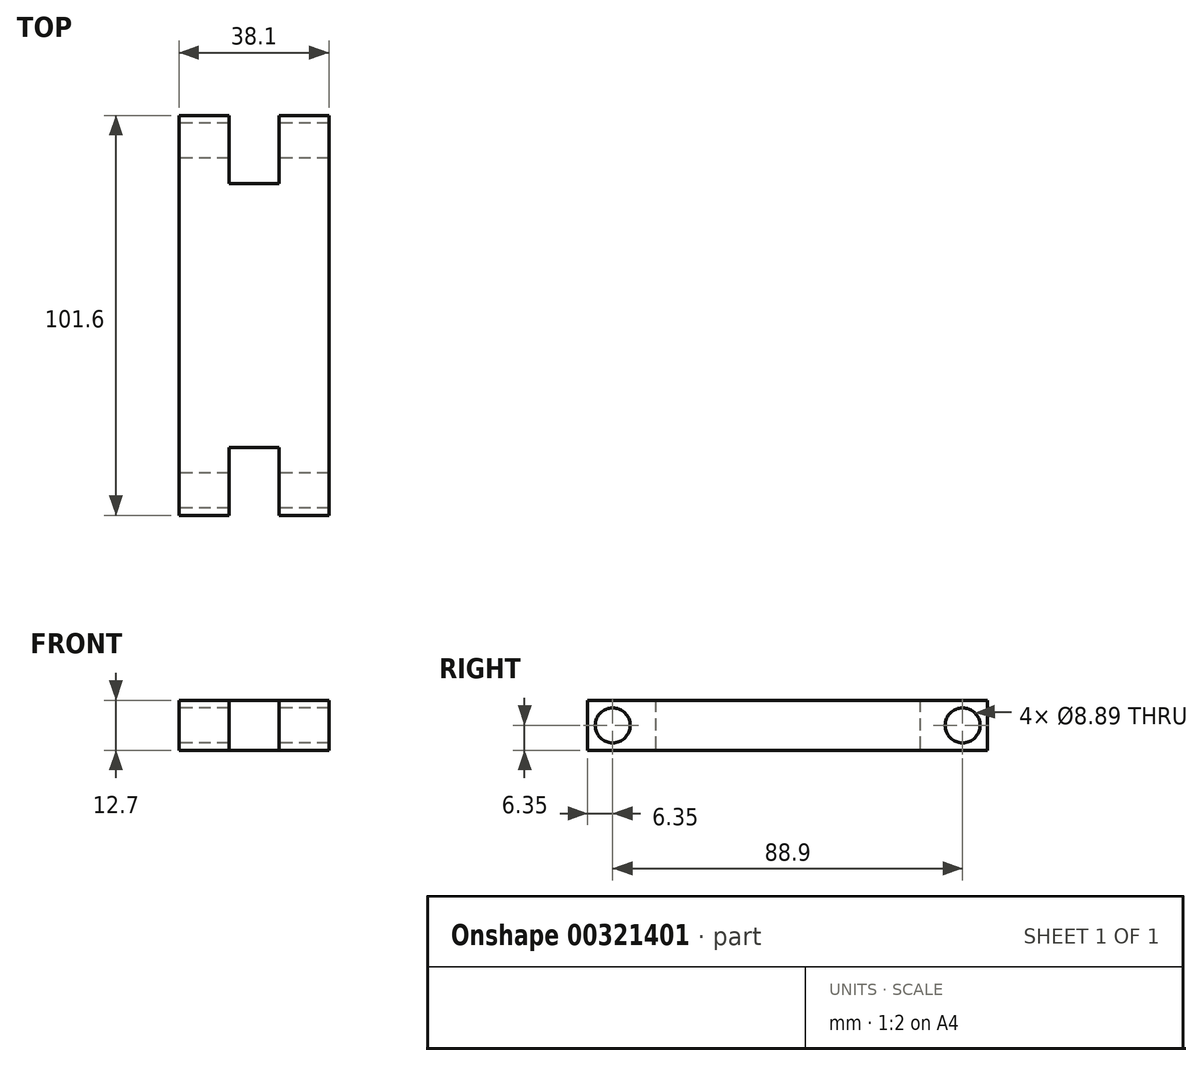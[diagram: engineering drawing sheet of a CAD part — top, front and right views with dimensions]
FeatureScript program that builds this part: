
annotation { "Feature Type Name" : "Feature", "Feature Type Description" : "" }
export const myFeature = defineFeature(function(context is Context, id is Id, definition is map)
    precondition{}
    {
        {
            var Q0;
            Q0=qCreatedBy(makeId("Top.planeOp"),FACE);
            var sketch = newSketch(context, id + "F0", { "sketchPlane" : qUnion([Q0])});
            skLineSegment(sketch, "E0.top", {"start": v(0, 50.8) * mm, "end": v(12.7, 50.8) * mm});
            skLineSegment(sketch, "E1.right", {"start": v(12.7, 50.8) * mm, "end": v(12.7, 33.56) * mm});
            skLineSegment(sketch, "E2.bottom", {"start": v(38.1, 50.8) * mm, "end": v(25.4, 50.8) * mm});
            skLineSegment(sketch, "E2.right", {"start": v(25.4, 50.8) * mm, "end": v(25.4, 33.56) * mm});
            skLineSegment(sketch, "E3.trimOffspring", {"start": v(25.4, 50.8) * mm, "end": v(38.1, 50.8) * mm});
            skLineSegment(sketch, "E4", {"start": v(12.7, 33.56) * mm, "end": v(25.4, 33.56) * mm});
            skLineSegment(sketch, "E5.MirrorCS", {"start": v(0, -50.8) * mm, "end": v(12.7, -50.8) * mm});
            skLineSegment(sketch, "E6.MirrorCS", {"start": v(12.7, -50.8) * mm, "end": v(12.7, -33.56) * mm});
            skLineSegment(sketch, "E7.MirrorCS", {"start": v(12.7, -33.56) * mm, "end": v(25.4, -33.56) * mm});
            skLineSegment(sketch, "E8.MirrorCS", {"start": v(25.4, -50.8) * mm, "end": v(25.4, -33.56) * mm});
            skLineSegment(sketch, "E9.MirrorCS", {"start": v(25.4, -50.8) * mm, "end": v(38.1, -50.8) * mm});
            skLineSegment(sketch, "E10", {"start": v(0, 50.8) * mm, "end": v(0, -50.8) * mm});
            skLineSegment(sketch, "E11", {"start": v(38.1, 50.8) * mm, "end": v(38.1, -50.8) * mm});
            skSolve(sketch);
        }
        {
            var Q0;
            Q0 = qSketchRegion(id + "F0", true);
            extrude(context, id + "F1", {"entities" : qUnion([Q0]), "depth" : 12.7 * mm});
        }
        {
            var Q0;
            Q0=makeQuery(id+"F1.opExtrude","SWEPT_FACE",FACE,{"disambiguationData":[OSD([sQuery(id+"F0.wireOp",EDGE,"E10")])]});
            var sketch = newSketch(context, id + "F2", { "sketchPlane" : qUnion([Q0])});
            skCircle(sketch, "E12", {"center": v(-44.45, 6.35) * mm, "radius": 4.45 * mm});
            skPoint(sketch, "E12.centerSnap0", {"position": v(-50.8, 6.35) * mm});
            skCircle(sketch, "E13", {"center": v(44.45, 6.35) * mm, "radius": 4.45 * mm});
            skPoint(sketch, "E13.centerSnap0", {"position": v(50.8, 6.35) * mm});
            skSolve(sketch);
        }
        {
            var Q0;
            Q0 = qSketchRegion(id + "F2", true);
            var Q1;
            Q1=makeQuery(id+"F1.opExtrude","SWEPT_FACE",FACE,{"disambiguationData":[OSD([sQuery(id+"F0.wireOp",EDGE,"E11")])]});
            extrude(context, id + "F3", {"entities" : qUnion([Q0]), "operationType" : NewBodyOperationType.REMOVE, "endBound" : BoundingType.UP_TO_SURFACE, "oppositeDirection" : true, "endBoundEntityFace" : qUnion([Q1]), "depth" : 25.4 * mm});
        }
    });
